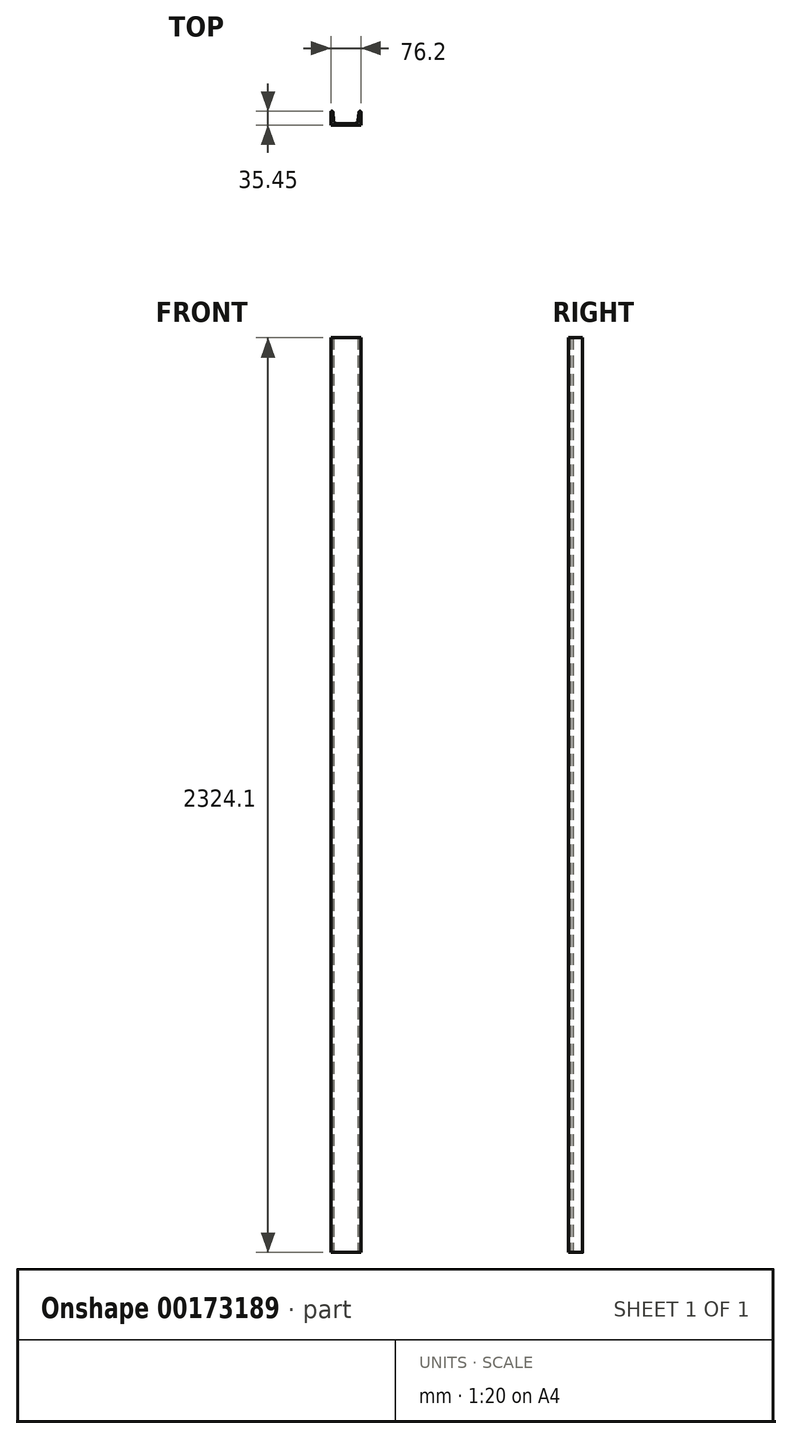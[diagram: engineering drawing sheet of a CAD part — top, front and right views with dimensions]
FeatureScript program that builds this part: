
annotation { "Feature Type Name" : "Feature", "Feature Type Description" : "" }
export const myFeature = defineFeature(function(context is Context, id is Id, definition is map)
    precondition{}
    {
        {
            var Q0;
            Q0=qCreatedBy(makeId("Top.planeOp"),FACE);
            var sketch = newSketch(context, id + "F0", { "sketchPlane" : qUnion([Q0])});
            skLineSegment(sketch, "E0", {"start": v(-33.57, 0) * mm, "end": v(42.63, 0) * mm});
            skLineSegment(sketch, "E1", {"start": v(42.63, 0) * mm, "end": v(42.63, 32.96) * mm});
            skLineSegment(sketch, "E2", {"start": v(-33.57, 0) * mm, "end": v(-33.57, 32.96) * mm});
            skLineSegment(sketch, "E3.0", {"start": v(-19.53, 4.34) * mm, "end": v(28.58, 4.34) * mm});
            skArc(sketch, "E4.filletArc", {"start": v(-26.64, 11.46) * mm, "mid": v(-24.56, 6.43) * mm, "end": v(-19.53, 4.34) * mm});
            skArc(sketch, "E5.filletArc", {"start": v(28.58, 4.34) * mm, "mid": v(33.6, 6.43) * mm, "end": v(35.7, 11.46) * mm});
            skLineSegment(sketch, "E6", {"start": v(-28.59, 33.18) * mm, "end": v(-26.64, 11.46) * mm});
            skLineSegment(sketch, "E7", {"start": v(35.7, 11.46) * mm, "end": v(37.64, 33.18) * mm});
            skArc(sketch, "E8.filletArc", {"start": v(-28.59, 33.18) * mm, "mid": v(-31.19, 35.45) * mm, "end": v(-33.57, 32.96) * mm});
            skArc(sketch, "E9.filletArc", {"start": v(42.63, 32.96) * mm, "mid": v(40.24, 35.45) * mm, "end": v(37.64, 33.18) * mm});
            skSolve(sketch);
        }
        {
            var Q0;
            Q0=makeQuery(id+"F0.imprint","IMPRINT",FACE,{"disambiguationData":[TD([[makeQuery(id+"F0.imprint","IMPRINT",EDGE,{"derivedFrom":sQuery(id+"F0.wireOp",EDGE,"E0")}),1.0]])]});
            extrude(context, id + "F1", {"entities" : qUnion([Q0]), "depth" : 2324.1 * mm});
        }
    });
